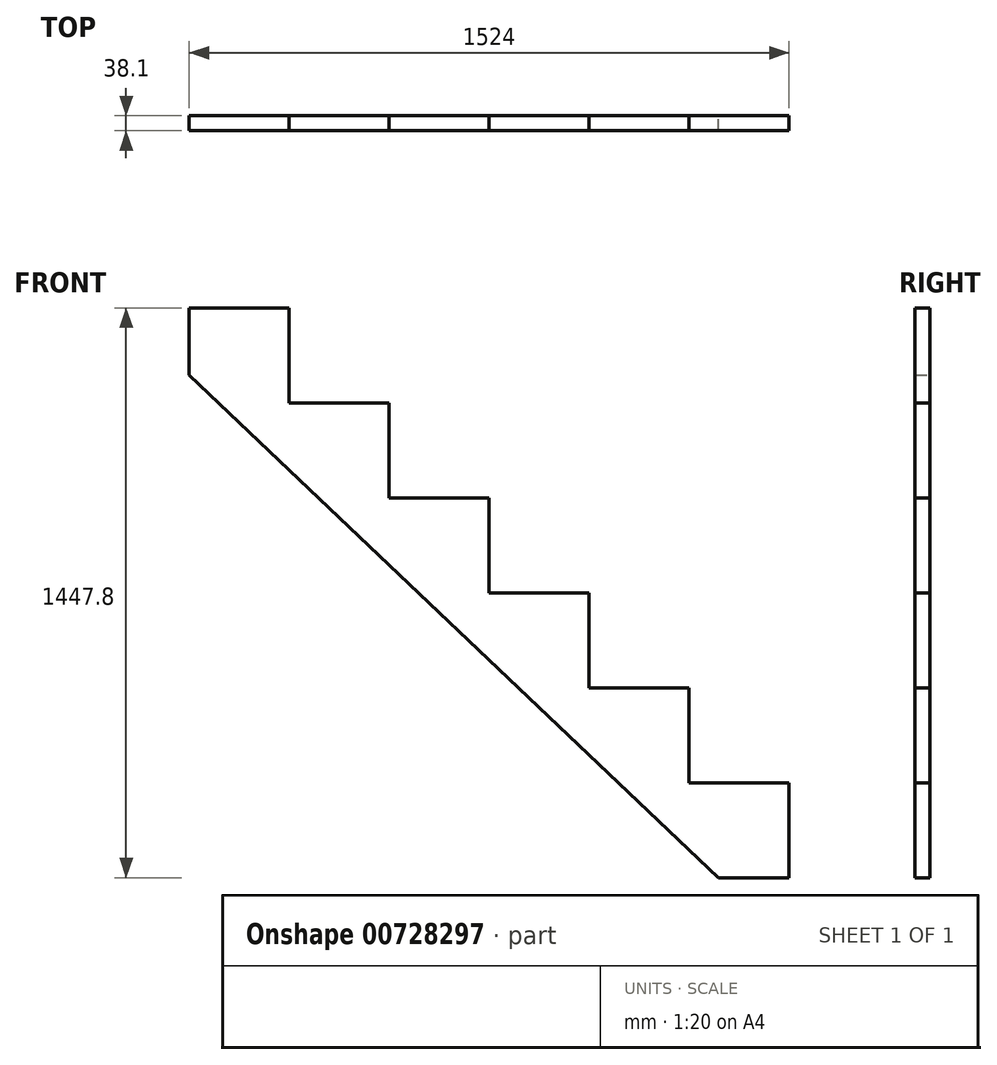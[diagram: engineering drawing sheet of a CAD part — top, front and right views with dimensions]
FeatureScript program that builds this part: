
annotation { "Feature Type Name" : "Feature", "Feature Type Description" : "" }
export const myFeature = defineFeature(function(context is Context, id is Id, definition is map)
    precondition{}
    {
        {
            var Q0;
            Q0=qCreatedBy(makeId("Front.planeOp"),FACE);
            var sketch = newSketch(context, id + "F0", { "sketchPlane" : qUnion([Q0])});
            skLineSegment(sketch, "E0", {"start": v(-899.88, 10483.2) * mm, "end": v(-899.88, 10312.84) * mm, "construction": true});
            skLineSegment(sketch, "E1", {"start": v(624.12, 9035.4) * mm, "end": v(624.12, 9276.7) * mm, "construction": true});
            skLineSegment(sketch, "E2", {"start": v(-899.88, 10483.2) * mm, "end": v(-645.88, 10483.2) * mm});
            skLineSegment(sketch, "E3", {"start": v(-645.88, 10483.2) * mm, "end": v(-645.88, 10241.9) * mm});
            skLineSegment(sketch, "E4", {"start": v(-645.88, 10241.9) * mm, "end": v(-391.88, 10241.9) * mm});
            skLineSegment(sketch, "E5", {"start": v(-391.88, 10241.9) * mm, "end": v(-391.88, 10000.6) * mm});
            skLineSegment(sketch, "E6", {"start": v(-391.88, 10000.6) * mm, "end": v(-137.88, 10000.6) * mm});
            skLineSegment(sketch, "E7", {"start": v(-137.88, 10000.6) * mm, "end": v(-137.88, 9759.3) * mm});
            skLineSegment(sketch, "E8", {"start": v(-137.88, 9759.3) * mm, "end": v(116.12, 9759.3) * mm});
            skLineSegment(sketch, "E9", {"start": v(116.12, 9759.3) * mm, "end": v(116.12, 9518) * mm});
            skLineSegment(sketch, "E10", {"start": v(116.12, 9518) * mm, "end": v(370.12, 9518) * mm});
            skLineSegment(sketch, "E11", {"start": v(370.12, 9518) * mm, "end": v(370.12, 9276.7) * mm});
            skLineSegment(sketch, "E12", {"start": v(370.12, 9276.7) * mm, "end": v(624.12, 9276.7) * mm});
            skLineSegment(sketch, "E13", {"start": v(624.12, 9276.7) * mm, "end": v(624.12, 9035.4) * mm});
            skLineSegment(sketch, "E14", {"start": v(-899.88, 10312.84) * mm, "end": v(444.8, 9035.4) * mm});
            skLineSegment(sketch, "E15", {"start": v(624.12, 9035.4) * mm, "end": v(444.8, 9035.4) * mm});
            skLineSegment(sketch, "E16", {"start": v(-899.88, 10483.2) * mm, "end": v(-899.88, 10312.84) * mm});
            skSolve(sketch);
        }
        {
            var Q0;
            Q0=qSketchRegion(id+"F0",true);
            extrude(context, id + "F1", {"entities" : qUnion([Q0]), "depth" : 38.1 * mm, "offsetDistance" : 25.4 * mm});
        }
    });
